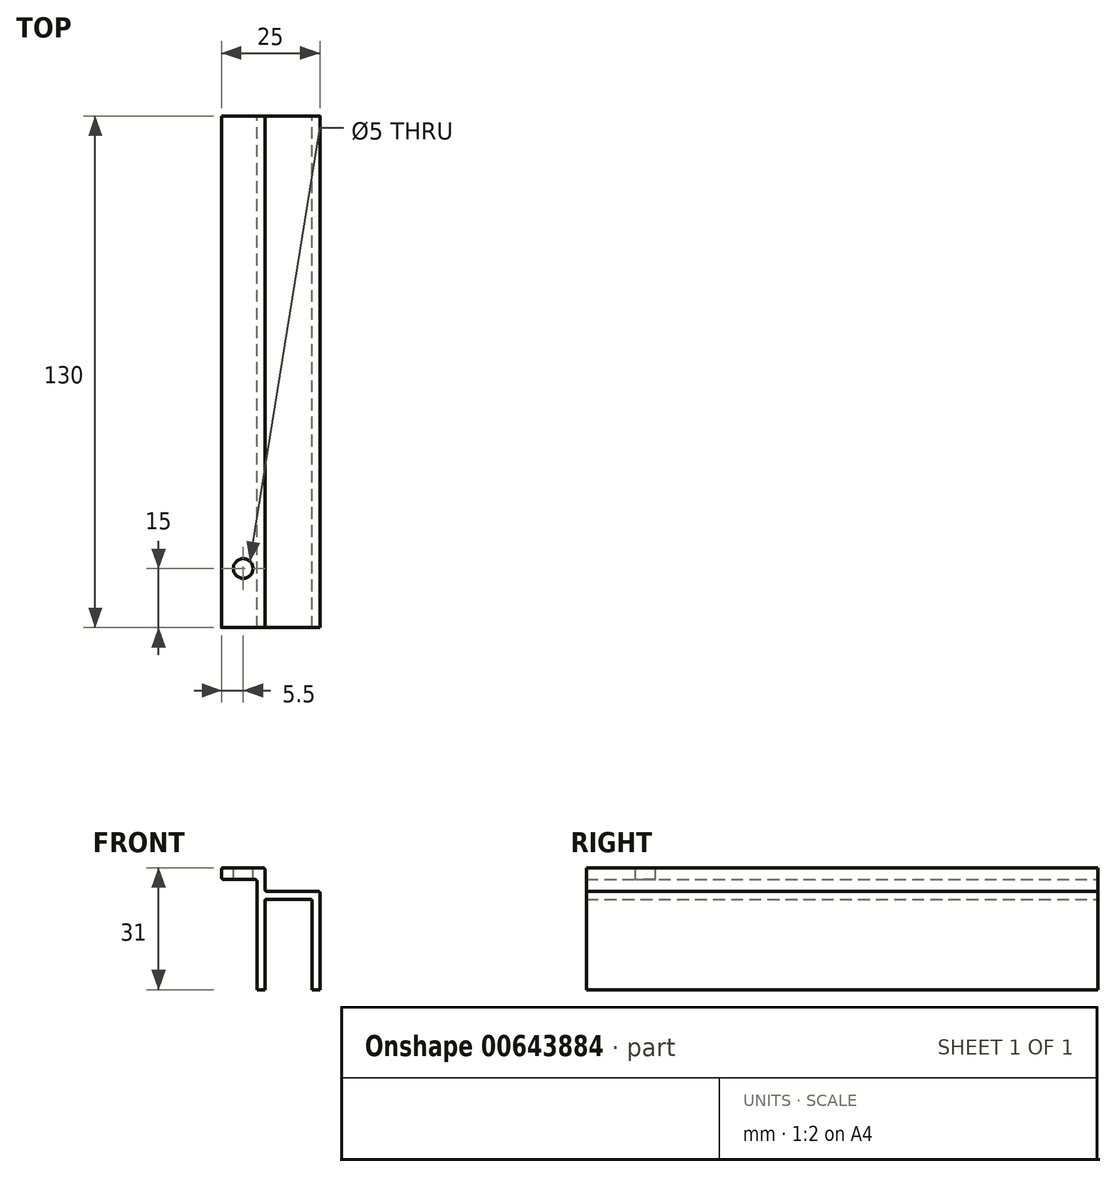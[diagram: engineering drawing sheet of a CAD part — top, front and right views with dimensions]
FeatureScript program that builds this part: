
annotation { "Feature Type Name" : "Feature", "Feature Type Description" : "" }
export const myFeature = defineFeature(function(context is Context, id is Id, definition is map)
    precondition{}
    {
        {
            var Q0;
            Q0=qCreatedBy(makeId("Front.planeOp"),FACE);
            var sketch = newSketch(context, id + "F0", { "sketchPlane" : qUnion([Q0])});
            skLineSegment(sketch, "E0", {"start": v(0, 0) * mm, "end": v(0, 24.5) * mm});
            skArc(sketch, "E1", {"start": v(0, 24.5) * mm, "mid": v(-0.15, 24.85) * mm, "end": v(-0.5, 25) * mm});
            skLineSegment(sketch, "E2", {"start": v(-2, 0) * mm, "end": v(-2, 22.5) * mm});
            skArc(sketch, "E3", {"start": v(-2, 22.5) * mm, "mid": v(-2.15, 22.85) * mm, "end": v(-2.5, 23) * mm});
            skLineSegment(sketch, "E4", {"start": v(-0.5, 25) * mm, "end": v(-13.5, 25) * mm});
            skLineSegment(sketch, "E5", {"start": v(-2, 0) * mm, "end": v(0, 0) * mm});
            skArc(sketch, "E6", {"start": v(-14, 25.5) * mm, "mid": v(-13.85, 25.15) * mm, "end": v(-13.5, 25) * mm});
            skArc(sketch, "E7", {"start": v(-14, 30.5) * mm, "mid": v(-14.15, 30.85) * mm, "end": v(-14.5, 31) * mm});
            skArc(sketch, "E8", {"start": v(-24.5, 31) * mm, "mid": v(-24.85, 30.85) * mm, "end": v(-25, 30.5) * mm});
            skLineSegment(sketch, "E9", {"start": v(-24.5, 31) * mm, "end": v(-14.5, 31) * mm});
            skLineSegment(sketch, "E10", {"start": v(-14, 30.5) * mm, "end": v(-14, 25.5) * mm});
            skLineSegment(sketch, "E11", {"start": v(-2.5, 23) * mm, "end": v(-13.5, 23) * mm});
            skLineSegment(sketch, "E12", {"start": v(-5.34, 25) * mm, "end": v(-5.34, 23) * mm, "construction": true});
            skLineSegment(sketch, "E13", {"start": v(-25, 30.5) * mm, "end": v(-25, 28.5) * mm});
            skArc(sketch, "E14", {"start": v(-25, 28.5) * mm, "mid": v(-24.85, 28.15) * mm, "end": v(-24.5, 28) * mm});
            skLineSegment(sketch, "E15", {"start": v(-24.5, 28) * mm, "end": v(-16.5, 28) * mm});
            skLineSegment(sketch, "E16", {"start": v(-16, 0) * mm, "end": v(-16, 27.5) * mm});
            skArc(sketch, "E17", {"start": v(-16, 27.5) * mm, "mid": v(-16.15, 27.85) * mm, "end": v(-16.5, 28) * mm});
            skLineSegment(sketch, "E18", {"start": v(-16, 27.05) * mm, "end": v(-14, 27.05) * mm, "construction": true});
            skLineSegment(sketch, "E19", {"start": v(-16, 0) * mm, "end": v(-14, 0) * mm});
            skLineSegment(sketch, "E20", {"start": v(-14, 0) * mm, "end": v(-14, 22.5) * mm});
            skArc(sketch, "E21", {"start": v(-13.5, 23) * mm, "mid": v(-13.85, 22.85) * mm, "end": v(-14, 22.5) * mm});
            skSolve(sketch);
        }
        {
            var Q0;
            Q0=qSketchRegion(id+"F0",true);
            extrude(context, id + "F1", {"entities" : qUnion([Q0]), "depth" : 130 * mm, "offsetDistance" : 25 * mm});
        }
        {
            var Q0;
            Q0=makeQuery(id+"F1.opExtrude","SWEPT_FACE",FACE,{"disambiguationData":[OSD([sQuery(id+"F0.wireOp",EDGE,"E9")])]});
            var sketch = newSketch(context, id + "F2", { "sketchPlane" : qUnion([Q0])});
            skPoint(sketch, "E22", {"position": v(-19.5, -115) * mm});
            skSolve(sketch);
        }
        {
            var Q0;
            Q0=sQuery(id+"F2.wireOp",VERTEX,"E22");
            var Q1;
            Q1=makeQuery(id+"F1.opExtrude","SWEPT_BODY",BODY,{"disambiguationData":[OSD([sQuery(id+"F0.wireOp",EDGE,"E0"),sQuery(id+"F0.wireOp",EDGE,"E1"),sQuery(id+"F0.wireOp",EDGE,"E2"),sQuery(id+"F0.wireOp",EDGE,"E3"),sQuery(id+"F0.wireOp",EDGE,"2dDcRPPx-qWLS-3jfH-2Z5e-5Ey4nYpIB2EE"),sQuery(id+"F0.wireOp",EDGE,"v6giGO9J-cYN8-t5IA-4Td5-0sDXakfVn9Gq"),sQuery(id+"F0.wireOp",EDGE,"Gdmqkj1D-Tf8d-NE69-CWPL-D2tNtE2yXyFt"),sQuery(id+"F0.wireOp",EDGE,"Ra4JJmEf-WoTX-qRGX-wUwy-kwYvwXnb2mAW"),sQuery(id+"F0.wireOp",EDGE,"E4"),sQuery(id+"F0.wireOp",EDGE,"KTlmZnO1-OWA3-ypoo-lhcI-twz0w1B18LaK"),sQuery(id+"F0.wireOp",EDGE,"SD9WD1UN-mr2G-s0Mi-IJeY-DgMuUSGvttQB"),sQuery(id+"F0.wireOp",EDGE,"iWeMQVvX-vgyw-r2q7-QUPC-cTUXbdXrcEzG"),sQuery(id+"F0.wireOp",EDGE,"E5"),sQuery(id+"F0.wireOp",EDGE,"E6"),sQuery(id+"F0.wireOp",EDGE,"E7"),sQuery(id+"F0.wireOp",EDGE,"E8"),sQuery(id+"F0.wireOp",EDGE,"E9"),sQuery(id+"F0.wireOp",EDGE,"E10"),sQuery(id+"F0.wireOp",EDGE,"E11"),sQuery(id+"F0.wireOp",EDGE,"UNXbFQkl-fwZk-UQnE-xJBs-wBAvHsw7UyoN"),sQuery(id+"F0.wireOp",EDGE,"GrC9foEB-6BIC-XJ97-hV8U-eVDUel4D8yFU")])]});
            hole(context, id + "F3", {"style" : HoleStyle.SIMPLE, "endStyle" : HoleEndStyle.THROUGH, "holeDiameter" : 5 * mm, "majorDiameter" : 5 * mm, "isTappedThrough" : true, "tappedDepth" : 12 * mm, "tapClearance" : 3, "locations" : qUnion([Q0]), "scope" : qUnion([Q1])});
        }
    });
